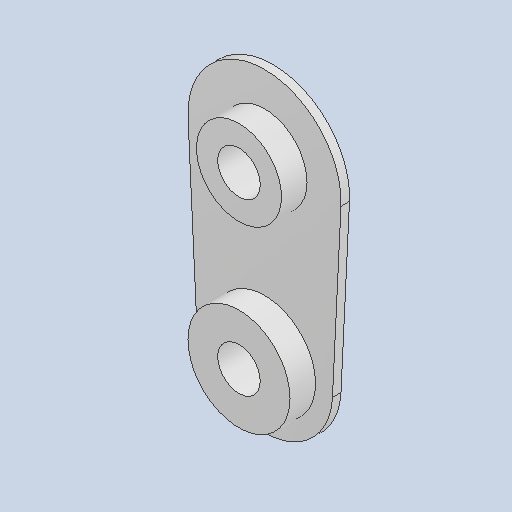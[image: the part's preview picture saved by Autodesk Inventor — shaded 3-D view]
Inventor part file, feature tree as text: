
AUTODESK INVENTOR PART (.ipt)
format: ipt  version: 2023 (Build 270158030, 158C)  size: 124,416 bytes
history: native  units: mm
features: extrude x2, sketch x1
ambient origin geometry x8: Origin, YZ Plane, XZ Plane, XY Plane, X Axis, Y Axis, Z Axis, Center Point
bodies: Solid1 (feature_tree)
feature tree (3):
  sketch  "Sketch1"  dims[d8=9.0mm d13=5.0mm d25=2.5mm d26=6.0mm d27=8.0mm d28=2.5mm d29=10.0mm d30=0.5mm d31=0.0mm d32=2.0mm d33=0.0mm]
  extrude  "Extrusion1"  Depth=10.0mm
  extrude  "Extrusion2"  Depth=0.5mm TaperAngle=0.0deg
